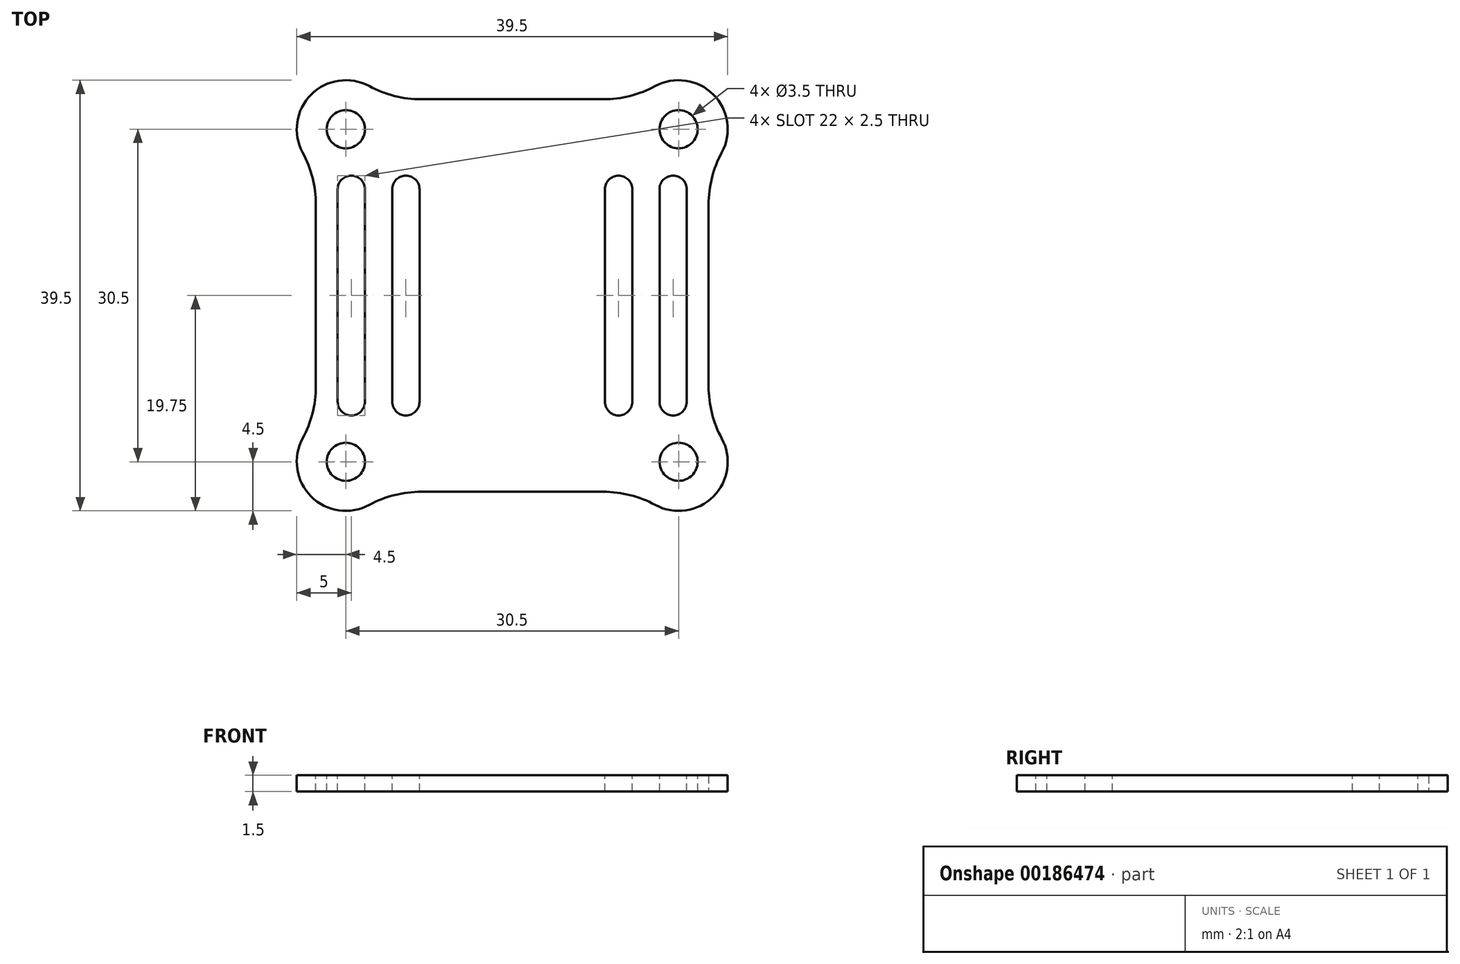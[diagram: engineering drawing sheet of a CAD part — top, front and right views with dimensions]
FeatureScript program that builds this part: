
annotation { "Feature Type Name" : "Feature", "Feature Type Description" : "" }
export const myFeature = defineFeature(function(context is Context, id is Id, definition is map)
    precondition{}
    {
        {
            var Q0;
            Q0=qCreatedBy(makeId("Top.planeOp"),FACE);
            var sketch = newSketch(context, id + "F0", { "sketchPlane" : qUnion([Q0])});
            skLineSegment(sketch, "E0.bottom", {"start": v(-18, 18) * mm, "end": v(18, 18) * mm});
            skLineSegment(sketch, "E0.top", {"start": v(-18, -18) * mm, "end": v(18, -18) * mm});
            skLineSegment(sketch, "E0.left", {"start": v(-18, 18) * mm, "end": v(-18, -18) * mm});
            skLineSegment(sketch, "E0.right", {"start": v(18, 18) * mm, "end": v(18, -18) * mm});
            skSolve(sketch);
        }
        {
            var Q0;
            Q0=qSketchRegion(id+"F0",true);
            extrude(context, id + "F1", {"entities" : qUnion([Q0]), "depth" : 1.5 * mm});
        }
        {
            var Q0;
            Q0=qCreatedBy(makeId("Top.planeOp"),FACE);
            var sketch = newSketch(context, id + "F2", { "sketchPlane" : qUnion([Q0])});
            skCircle(sketch, "E1.cCircle", {"center": v(-15.25, 15.25) * mm, "radius": 4.5 * mm});
            skCircle(sketch, "E2.MirrorC", {"center": v(15.25, 15.25) * mm, "radius": 4.5 * mm});
            skCircle(sketch, "E3.MirrorC", {"center": v(-15.25, -15.25) * mm, "radius": 4.5 * mm});
            skCircle(sketch, "E4.MirrorC", {"center": v(15.25, -15.25) * mm, "radius": 4.5 * mm});
            skSolve(sketch);
        }
        {
            var Q0;
            Q0=qSketchRegion(id+"F2",true);
            extrude(context, id + "F3", {"entities" : qUnion([Q0]), "operationType" : NewBodyOperationType.ADD, "depth" : 1.5 * mm});
        }
        {
            var Q0;
            Q0=makeQuery(id+"F3.boolean.opBoolean","MERGE",FACE,{"derivedFrom":[makeQuery(id+"F1.opExtrude","CAP_FACE",FACE,{"disambiguationData":[OSD([sQuery(id+"F0.wireOp",EDGE,"E0.bottom"),sQuery(id+"F0.wireOp",EDGE,"E0.top"),sQuery(id+"F0.wireOp",EDGE,"E0.left"),sQuery(id+"F0.wireOp",EDGE,"E0.right")])],"isStart":false}),makeQuery(id+"F3.opExtrude","CAP_FACE",FACE,{"disambiguationData":[OSD([sQuery(id+"F2.wireOp",EDGE,"E1.0"),sQuery(id+"F2.wireOp",EDGE,"E1.1"),sQuery(id+"F2.wireOp",EDGE,"E1.2"),sQuery(id+"F2.wireOp",EDGE,"E1.3"),sQuery(id+"F2.wireOp",EDGE,"E1.4"),sQuery(id+"F2.wireOp",EDGE,"E1.5")])],"isStart":false}),makeQuery(id+"F3.opExtrude","CAP_FACE",FACE,{"disambiguationData":[OSD([sQuery(id+"F2.wireOp",EDGE,"0616565c-09db-46bf-ad57-eb945f58c0542.MirrorCS"),sQuery(id+"F2.wireOp",EDGE,"0616565c-09db-46bf-ad57-eb945f58c0543.MirrorCS"),sQuery(id+"F2.wireOp",EDGE,"0616565c-09db-46bf-ad57-eb945f58c0544.MirrorCS"),sQuery(id+"F2.wireOp",EDGE,"0616565c-09db-46bf-ad57-eb945f58c0545.MirrorCS"),sQuery(id+"F2.wireOp",EDGE,"0616565c-09db-46bf-ad57-eb945f58c0546.MirrorCS"),sQuery(id+"F2.wireOp",EDGE,"NHSgZ3yU-8GIX-roRx-HkwB-HkZAcJlPE89G")])],"isStart":false}),makeQuery(id+"F3.opExtrude","CAP_FACE",FACE,{"disambiguationData":[OSD([sQuery(id+"F2.wireOp",EDGE,"2a467472-49c5-4a11-8a41-0fdfe6fb91940.MirrorCS"),sQuery(id+"F2.wireOp",EDGE,"2a467472-49c5-4a11-8a41-0fdfe6fb91941.MirrorCS"),sQuery(id+"F2.wireOp",EDGE,"2a467472-49c5-4a11-8a41-0fdfe6fb91944.MirrorCS"),sQuery(id+"F2.wireOp",EDGE,"2a467472-49c5-4a11-8a41-0fdfe6fb91946.MirrorCS"),sQuery(id+"F2.wireOp",EDGE,"2a467472-49c5-4a11-8a41-0fdfe6fb91948.MirrorCS"),sQuery(id+"F2.wireOp",EDGE,"2a467472-49c5-4a11-8a41-0fdfe6fb919414.MirrorCS")])],"isStart":false}),makeQuery(id+"F3.opExtrude","CAP_FACE",FACE,{"disambiguationData":[OSD([sQuery(id+"F2.wireOp",EDGE,"2a467472-49c5-4a11-8a41-0fdfe6fb91942.MirrorCS"),sQuery(id+"F2.wireOp",EDGE,"2a467472-49c5-4a11-8a41-0fdfe6fb91943.MirrorCS"),sQuery(id+"F2.wireOp",EDGE,"2a467472-49c5-4a11-8a41-0fdfe6fb91945.MirrorCS"),sQuery(id+"F2.wireOp",EDGE,"2a467472-49c5-4a11-8a41-0fdfe6fb91947.MirrorCS"),sQuery(id+"F2.wireOp",EDGE,"2a467472-49c5-4a11-8a41-0fdfe6fb91949.MirrorCS"),sQuery(id+"F2.wireOp",EDGE,"UI0glx2i-9ms3-tcvH-gTJu-MVt1pbo6Ya8X")])],"isStart":false})]});
            var sketch = newSketch(context, id + "F4", { "sketchPlane" : qUnion([Q0])});
            skCircle(sketch, "E5", {"center": v(-15.25, -15.25) * mm, "radius": 1.75 * mm});
            skCircle(sketch, "E6.MirrorC", {"center": v(15.25, -15.25) * mm, "radius": 1.75 * mm});
            skCircle(sketch, "E7.MirrorC", {"center": v(-15.25, 15.25) * mm, "radius": 1.75 * mm});
            skCircle(sketch, "E8.MirrorC", {"center": v(15.25, 15.25) * mm, "radius": 1.75 * mm});
            skSolve(sketch);
        }
        {
            var Q0;
            Q0 = qSketchRegion(id + "F4", true);
            extrude(context, id + "F5", {"entities" : qUnion([Q0]), "operationType" : NewBodyOperationType.REMOVE, "endBound" : BoundingType.THROUGH_ALL, "oppositeDirection" : true, "depth" : 25 * mm});
        }
        {
            var Q0;
            Q0=makeQuery(id+"F3.boolean.opBoolean","MERGE",FACE,{"derivedFrom":[makeQuery(id+"F1.opExtrude","CAP_FACE",FACE,{"disambiguationData":[OSD([sQuery(id+"F0.wireOp",EDGE,"E0.bottom"),sQuery(id+"F0.wireOp",EDGE,"E0.top"),sQuery(id+"F0.wireOp",EDGE,"E0.left"),sQuery(id+"F0.wireOp",EDGE,"E0.right")])],"isStart":false}),makeQuery(id+"F3.opExtrude","CAP_FACE",FACE,{"disambiguationData":[OSD([sQuery(id+"F2.wireOp",EDGE,"E1.cCircle")])],"isStart":false}),makeQuery(id+"F3.opExtrude","CAP_FACE",FACE,{"disambiguationData":[OSD([sQuery(id+"F2.wireOp",EDGE,"E2.MirrorC")])],"isStart":false}),makeQuery(id+"F3.opExtrude","CAP_FACE",FACE,{"disambiguationData":[OSD([sQuery(id+"F2.wireOp",EDGE,"E3.MirrorC")])],"isStart":false}),makeQuery(id+"F3.opExtrude","CAP_FACE",FACE,{"disambiguationData":[OSD([sQuery(id+"F2.wireOp",EDGE,"E4.MirrorC")])],"isStart":false})]});
            var sketch = newSketch(context, id + "F6", { "sketchPlane" : qUnion([Q0])});
            skLineSegment(sketch, "E9.bottom", {"start": v(-9.75, 11) * mm, "end": v(-9.75, 11) * mm});
            skLineSegment(sketch, "E9.top", {"start": v(-9.75, -11) * mm, "end": v(-9.75, -11) * mm});
            skLineSegment(sketch, "E9.left", {"start": v(-11, 9.75) * mm, "end": v(-11, -9.75) * mm});
            skLineSegment(sketch, "E9.right", {"start": v(-8.5, 9.75) * mm, "end": v(-8.5, -9.75) * mm});
            skLineSegment(sketch, "E10.bottom", {"start": v(-14.75, 11) * mm, "end": v(-14.75, 11) * mm});
            skLineSegment(sketch, "E10.top", {"start": v(-14.75, -11) * mm, "end": v(-14.75, -11) * mm});
            skLineSegment(sketch, "E10.left", {"start": v(-16, 9.75) * mm, "end": v(-16, -9.75) * mm});
            skLineSegment(sketch, "E10.right", {"start": v(-13.5, 9.75) * mm, "end": v(-13.5, -9.75) * mm});
            skLineSegment(sketch, "E11.MirrorCS", {"start": v(8.5, 9.75) * mm, "end": v(8.5, -9.75) * mm});
            skLineSegment(sketch, "E12.MirrorCS", {"start": v(14.75, -11) * mm, "end": v(14.75, -11) * mm});
            skLineSegment(sketch, "E13.MirrorCS", {"start": v(16, 9.75) * mm, "end": v(16, -9.75) * mm});
            skLineSegment(sketch, "E14.MirrorCS", {"start": v(14.75, 11) * mm, "end": v(14.75, 11) * mm});
            skLineSegment(sketch, "E15.MirrorCS", {"start": v(11, 9.75) * mm, "end": v(11, -9.75) * mm});
            skLineSegment(sketch, "E16.MirrorCS", {"start": v(9.75, 11) * mm, "end": v(9.75, 11) * mm});
            skLineSegment(sketch, "E17.MirrorCS", {"start": v(9.75, -11) * mm, "end": v(9.75, -11) * mm});
            skLineSegment(sketch, "E18.MirrorCS", {"start": v(13.5, 9.75) * mm, "end": v(13.5, -9.75) * mm});
            skPoint(sketch, "E19.visualSharp", {"position": v(-16, 11) * mm});
            skArc(sketch, "E19.filletArc", {"start": v(-14.75, 11) * mm, "mid": v(-15.63, 10.63) * mm, "end": v(-16, 9.75) * mm});
            skPoint(sketch, "E20.visualSharp", {"position": v(-13.5, 11) * mm});
            skArc(sketch, "E20.filletArc", {"start": v(-13.5, 9.75) * mm, "mid": v(-13.87, 10.63) * mm, "end": v(-14.75, 11) * mm});
            skPoint(sketch, "E21.visualSharp", {"position": v(-16, -11) * mm});
            skArc(sketch, "E21.filletArc", {"start": v(-16, -9.75) * mm, "mid": v(-15.63, -10.63) * mm, "end": v(-14.75, -11) * mm});
            skPoint(sketch, "E22.visualSharp", {"position": v(-13.5, -11) * mm});
            skArc(sketch, "E22.filletArc", {"start": v(-14.75, -11) * mm, "mid": v(-13.87, -10.63) * mm, "end": v(-13.5, -9.75) * mm});
            skPoint(sketch, "E23.visualSharp", {"position": v(-11, -11) * mm});
            skArc(sketch, "E23.filletArc", {"start": v(-11, -9.75) * mm, "mid": v(-10.63, -10.63) * mm, "end": v(-9.75, -11) * mm});
            skPoint(sketch, "E24.visualSharp", {"position": v(-8.5, -11) * mm});
            skArc(sketch, "E24.filletArc", {"start": v(-9.75, -11) * mm, "mid": v(-8.87, -10.63) * mm, "end": v(-8.5, -9.75) * mm});
            skPoint(sketch, "E25.visualSharp", {"position": v(8.5, -11) * mm});
            skArc(sketch, "E25.filletArc", {"start": v(8.5, -9.75) * mm, "mid": v(8.87, -10.63) * mm, "end": v(9.75, -11) * mm});
            skPoint(sketch, "E26.visualSharp", {"position": v(13.5, -11) * mm});
            skArc(sketch, "E26.filletArc", {"start": v(13.5, -9.75) * mm, "mid": v(13.87, -10.63) * mm, "end": v(14.75, -11) * mm});
            skPoint(sketch, "E27.visualSharp", {"position": v(11, -11) * mm});
            skArc(sketch, "E27.filletArc", {"start": v(9.75, -11) * mm, "mid": v(10.63, -10.63) * mm, "end": v(11, -9.75) * mm});
            skPoint(sketch, "E28.visualSharp", {"position": v(16, -11) * mm});
            skArc(sketch, "E28.filletArc", {"start": v(14.75, -11) * mm, "mid": v(15.63, -10.63) * mm, "end": v(16, -9.75) * mm});
            skPoint(sketch, "E29.visualSharp", {"position": v(-11, 11) * mm});
            skArc(sketch, "E29.filletArc", {"start": v(-9.75, 11) * mm, "mid": v(-10.63, 10.63) * mm, "end": v(-11, 9.75) * mm});
            skPoint(sketch, "E30.visualSharp", {"position": v(8.5, 11) * mm});
            skArc(sketch, "E30.filletArc", {"start": v(9.75, 11) * mm, "mid": v(8.87, 10.63) * mm, "end": v(8.5, 9.75) * mm});
            skPoint(sketch, "E31.visualSharp", {"position": v(13.5, 11) * mm});
            skArc(sketch, "E31.filletArc", {"start": v(14.75, 11) * mm, "mid": v(13.87, 10.63) * mm, "end": v(13.5, 9.75) * mm});
            skPoint(sketch, "E32.visualSharp", {"position": v(-8.5, 11) * mm});
            skArc(sketch, "E32.filletArc", {"start": v(-8.5, 9.75) * mm, "mid": v(-8.87, 10.63) * mm, "end": v(-9.75, 11) * mm});
            skPoint(sketch, "E33.visualSharp", {"position": v(11, 11) * mm});
            skArc(sketch, "E33.filletArc", {"start": v(11, 9.75) * mm, "mid": v(10.63, 10.63) * mm, "end": v(9.75, 11) * mm});
            skPoint(sketch, "E34.visualSharp", {"position": v(16, 11) * mm});
            skArc(sketch, "E34.filletArc", {"start": v(16, 9.75) * mm, "mid": v(15.63, 10.63) * mm, "end": v(14.75, 11) * mm});
            skSolve(sketch);
        }
        {
            var Q0;
            Q0 = qSketchRegion(id + "F6", true);
            extrude(context, id + "F7", {"entities" : qUnion([Q0]), "operationType" : NewBodyOperationType.REMOVE, "endBound" : BoundingType.THROUGH_ALL, "oppositeDirection" : true, "depth" : 25 * mm});
        }
        {
            var Q0;
            Q0=makeQuery(id+"F3.boolean.opBoolean","INTERSECT",EDGE,{"derivedFrom":[makeQuery(id+"F1.opExtrude","SWEPT_FACE",FACE,{"disambiguationData":[OSD([sQuery(id+"F0.wireOp",EDGE,"E0.left")])]}),makeQuery(id+"F3.opExtrude","SWEPT_FACE",FACE,{"disambiguationData":[OSD([sQuery(id+"F2.wireOp",EDGE,"E1.cCircle")])]})]});
            var Q1;
            Q1=makeQuery(id+"F3.boolean.opBoolean","INTERSECT",EDGE,{"derivedFrom":[makeQuery(id+"F1.opExtrude","SWEPT_FACE",FACE,{"disambiguationData":[OSD([sQuery(id+"F0.wireOp",EDGE,"E0.bottom")])]}),makeQuery(id+"F3.opExtrude","SWEPT_FACE",FACE,{"disambiguationData":[OSD([sQuery(id+"F2.wireOp",EDGE,"E1.cCircle")])]})]});
            var Q2;
            Q2=makeQuery(id+"F3.boolean.opBoolean","INTERSECT",EDGE,{"derivedFrom":[makeQuery(id+"F1.opExtrude","SWEPT_FACE",FACE,{"disambiguationData":[OSD([sQuery(id+"F0.wireOp",EDGE,"E0.bottom")])]}),makeQuery(id+"F3.opExtrude","SWEPT_FACE",FACE,{"disambiguationData":[OSD([sQuery(id+"F2.wireOp",EDGE,"E2.MirrorC")])]})]});
            var Q3;
            Q3=makeQuery(id+"F3.boolean.opBoolean","INTERSECT",EDGE,{"derivedFrom":[makeQuery(id+"F1.opExtrude","SWEPT_FACE",FACE,{"disambiguationData":[OSD([sQuery(id+"F0.wireOp",EDGE,"E0.right")])]}),makeQuery(id+"F3.opExtrude","SWEPT_FACE",FACE,{"disambiguationData":[OSD([sQuery(id+"F2.wireOp",EDGE,"E2.MirrorC")])]})]});
            var Q4;
            Q4=makeQuery(id+"F3.boolean.opBoolean","INTERSECT",EDGE,{"derivedFrom":[makeQuery(id+"F1.opExtrude","SWEPT_FACE",FACE,{"disambiguationData":[OSD([sQuery(id+"F0.wireOp",EDGE,"E0.right")])]}),makeQuery(id+"F3.opExtrude","SWEPT_FACE",FACE,{"disambiguationData":[OSD([sQuery(id+"F2.wireOp",EDGE,"E4.MirrorC")])]})]});
            var Q5;
            Q5=makeQuery(id+"F3.boolean.opBoolean","INTERSECT",EDGE,{"derivedFrom":[makeQuery(id+"F1.opExtrude","SWEPT_FACE",FACE,{"disambiguationData":[OSD([sQuery(id+"F0.wireOp",EDGE,"E0.top")])]}),makeQuery(id+"F3.opExtrude","SWEPT_FACE",FACE,{"disambiguationData":[OSD([sQuery(id+"F2.wireOp",EDGE,"E4.MirrorC")])]})]});
            var Q6;
            Q6=makeQuery(id+"F3.boolean.opBoolean","INTERSECT",EDGE,{"derivedFrom":[makeQuery(id+"F1.opExtrude","SWEPT_FACE",FACE,{"disambiguationData":[OSD([sQuery(id+"F0.wireOp",EDGE,"E0.top")])]}),makeQuery(id+"F3.opExtrude","SWEPT_FACE",FACE,{"disambiguationData":[OSD([sQuery(id+"F2.wireOp",EDGE,"E3.MirrorC")])]})]});
            var Q7;
            Q7=makeQuery(id+"F3.boolean.opBoolean","INTERSECT",EDGE,{"derivedFrom":[makeQuery(id+"F1.opExtrude","SWEPT_FACE",FACE,{"disambiguationData":[OSD([sQuery(id+"F0.wireOp",EDGE,"E0.left")])]}),makeQuery(id+"F3.opExtrude","SWEPT_FACE",FACE,{"disambiguationData":[OSD([sQuery(id+"F2.wireOp",EDGE,"E3.MirrorC")])]})]});
            fillet(context, id + "F8", {"entities" : qUnion([Q0, Q1, Q2, Q3, Q4, Q5, Q6, Q7]), "radius" : 10 * mm, "tangentPropagation" : true, "allowEdgeOverflow" : false});
        }
    });
